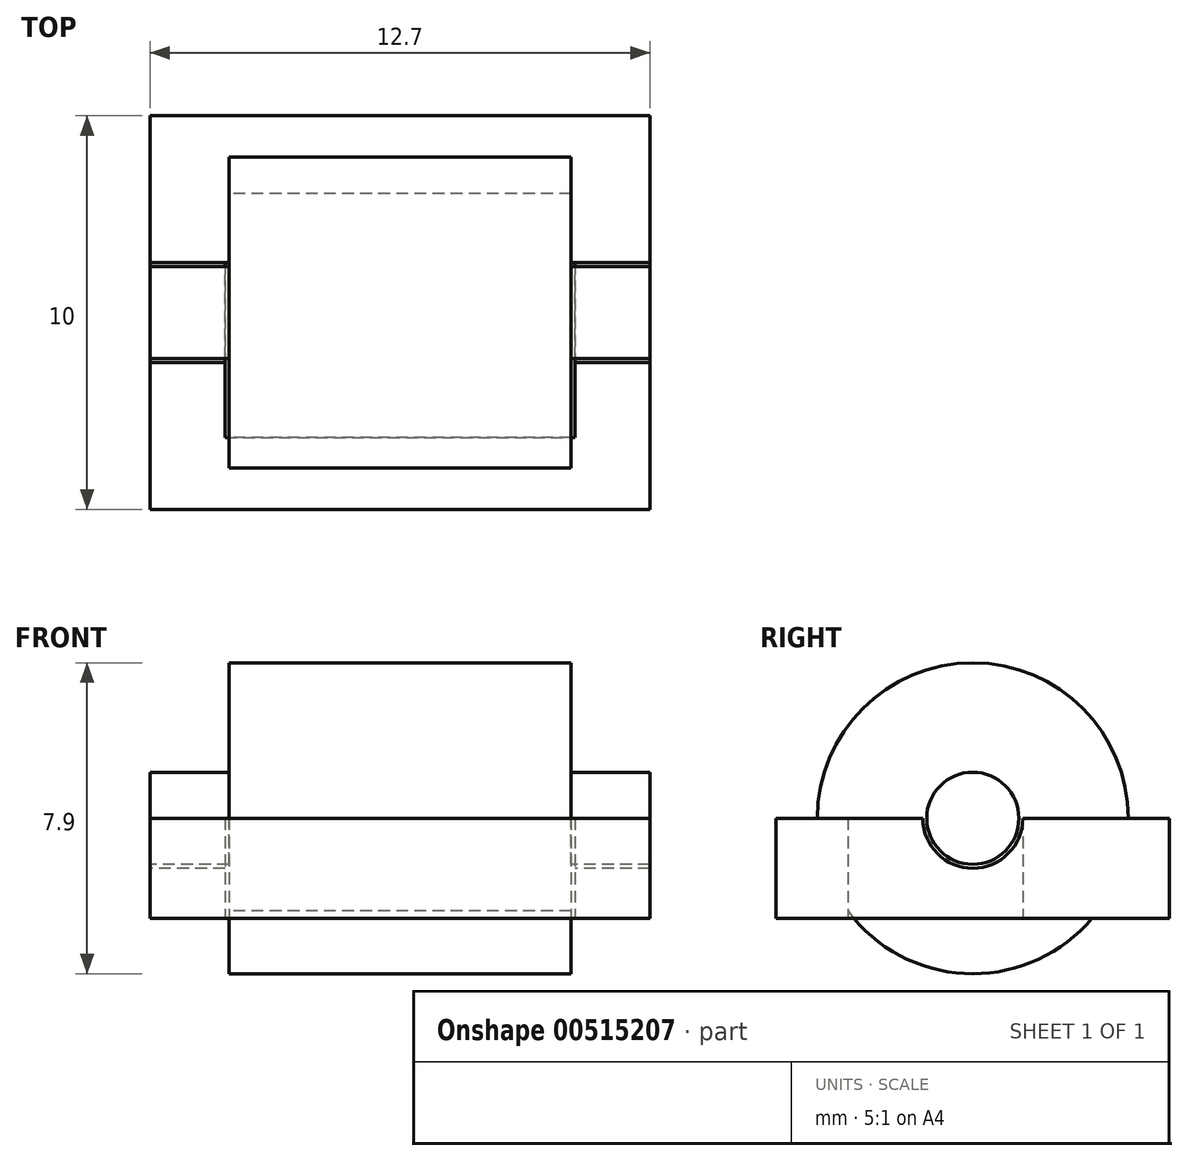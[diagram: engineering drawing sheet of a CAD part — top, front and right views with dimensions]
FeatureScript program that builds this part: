
annotation { "Feature Type Name" : "Feature", "Feature Type Description" : "" }
export const myFeature = defineFeature(function(context is Context, id is Id, definition is map)
    precondition{}
    {
        {
            var Q0;
            Q0=qCreatedBy(makeId("Right.planeOp"),FACE);
            var sketch = newSketch(context, id + "F0", { "sketchPlane" : qUnion([Q0])});
            skLineSegment(sketch, "E0", {"start": v(0, 0) * mm, "end": v(5, 0) * mm});
            skLineSegment(sketch, "E1", {"start": v(5, 0) * mm, "end": v(5, 2.54) * mm});
            skLineSegment(sketch, "E2", {"start": v(5, 2.54) * mm, "end": v(1.27, 2.54) * mm});
            skLineSegment(sketch, "E3", {"start": v(0, 0) * mm, "end": v(-5, 0) * mm});
            skLineSegment(sketch, "E4", {"start": v(-5, 0) * mm, "end": v(-5, 2.54) * mm});
            skLineSegment(sketch, "E5", {"start": v(-5, 2.54) * mm, "end": v(-1.27, 2.54) * mm});
            skArc(sketch, "E6", {"start": v(-1.27, 2.54) * mm, "mid": v(0, 1.27) * mm, "end": v(1.27, 2.54) * mm});
            skLineSegment(sketch, "E7", {"start": v(-1.27, 2.54) * mm, "end": v(1.27, 2.54) * mm, "construction": true});
            skSolve(sketch);
        }
        {
            var Q0;
            Q0=makeQuery(id+"F0.imprint","IMPRINT",FACE,{"disambiguationData":[TD([[makeQuery(id+"F0.imprint","IMPRINT",EDGE,{"derivedFrom":sQuery(id+"F0.wireOp",EDGE,"E0")}),1.0]])]});
            extrude(context, id + "F1", {"entities" : qUnion([Q0]), "depth" : 6.35 * mm, "offsetDistance" : 25.4 * mm, "hasSecondDirection" : true, "secondDirectionOppositeDirection" : true, "secondDirectionDepth" : 6.35 * mm});
        }
        {
            var Q0;
            Q0=qCreatedBy(makeId("Top.planeOp"),FACE);
            var sketch = newSketch(context, id + "F2", { "sketchPlane" : qUnion([Q0])});
            skPoint(sketch, "E8.0", {"position": v(6.35, -1.27) * mm});
            skPoint(sketch, "E8.1", {"position": v(-6.35, 1.27) * mm});
            skLineSegment(sketch, "E9", {"start": v(6.35, -1.27) * mm, "end": v(4.45, -1.27) * mm});
            skLineSegment(sketch, "E10", {"start": v(-6.35, 1.27) * mm, "end": v(-4.45, 1.27) * mm});
            skLineSegment(sketch, "E11.bottom", {"start": v(-4.45, 1.27) * mm, "end": v(4.45, 1.27) * mm});
            skLineSegment(sketch, "E11.top", {"start": v(-4.45, -1.27) * mm, "end": v(4.45, -1.27) * mm});
            skLineSegment(sketch, "E11.left", {"start": v(-4.45, 1.27) * mm, "end": v(-4.45, -1.27) * mm});
            skLineSegment(sketch, "E11.right", {"start": v(4.45, 1.27) * mm, "end": v(4.45, -1.27) * mm});
            skLineSegment(sketch, "E12", {"start": v(4.45, -1.27) * mm, "end": v(4.45, -3.18) * mm, "construction": true});
            skLineSegment(sketch, "E13", {"start": v(-4.45, 1.27) * mm, "end": v(-4.45, 3.18) * mm, "construction": true});
            skLineSegment(sketch, "E14.top", {"start": v(-4.45, -3.18) * mm, "end": v(4.45, -3.18) * mm});
            skLineSegment(sketch, "E14.left", {"start": v(-4.45, -1.27) * mm, "end": v(-4.45, -3.18) * mm});
            skLineSegment(sketch, "E14.right", {"start": v(4.45, -1.27) * mm, "end": v(4.45, -3.18) * mm});
            skLineSegment(sketch, "E15.bottom", {"start": v(4.45, 1.27) * mm, "end": v(-4.45, 1.27) * mm});
            skLineSegment(sketch, "E15.top", {"start": v(4.45, 3.18) * mm, "end": v(-4.45, 3.18) * mm});
            skLineSegment(sketch, "E15.left", {"start": v(4.45, 1.27) * mm, "end": v(4.45, 3.18) * mm});
            skLineSegment(sketch, "E15.right", {"start": v(-4.45, 1.27) * mm, "end": v(-4.45, 3.18) * mm});
            skSolve(sketch);
        }
        {
            var Q0;
            Q0=makeQuery(id+"F2.imprint","IMPRINT",FACE,{"disambiguationData":[TD([[makeQuery(id+"F2.imprint","IMPRINT",EDGE,{"derivedFrom":sQuery(id+"F2.wireOp",EDGE,"E11.top")}),-1.0]])]});
            var Q1;
            Q1=makeQuery(id+"F2.imprint","IMPRINT",FACE,{"disambiguationData":[TD([[makeQuery(id+"F2.imprint","IMPRINT",EDGE,{"derivedFrom":sQuery(id+"F2.wireOp",EDGE,"E11.left")}),1.0]])]});
            var Q2;
            Q2=makeQuery(id+"F2.imprint","IMPRINT",FACE,{"disambiguationData":[TD([[makeQuery(id+"F2.imprint","IMPRINT",EDGE,{"derivedFrom":sQuery(id+"F2.wireOp",EDGE,"E15.bottom")}),-1.0]])]});
            extrude(context, id + "F3", {"entities" : qUnion([Q0, Q1, Q2]), "operationType" : NewBodyOperationType.REMOVE, "endBound" : BoundingType.UP_TO_NEXT, "depth" : 25.4 * mm, "offsetDistance" : 25.4 * mm});
        }
        {
            var Q0;
            Q0=qCreatedBy(makeId("Right.planeOp"),FACE);
            var sketch = newSketch(context, id + "F4", { "sketchPlane" : qUnion([Q0])});
            skArc(sketch, "E16.0", {"start": v(-1.27, 2.54) * mm, "mid": v(0, 1.27) * mm, "end": v(1.27, 2.54) * mm, "construction": true});
            skCircle(sketch, "E17", {"center": v(0, 2.54) * mm, "radius": 1.17 * mm});
            skSolve(sketch);
        }
        {
            var Q0;
            Q0 = qSketchRegion(id + "F4", true);
            extrude(context, id + "F5", {"entities" : qUnion([Q0]), "depth" : 6.35 * mm, "offsetDistance" : 25.4 * mm, "hasSecondDirection" : true, "secondDirectionOppositeDirection" : true, "secondDirectionDepth" : 6.35 * mm});
        }
        {
            var Q0;
            Q0=qCreatedBy(makeId("Right.planeOp"),FACE);
            var sketch = newSketch(context, id + "F6", { "sketchPlane" : qUnion([Q0])});
            skPoint(sketch, "E18.0", {"position": v(-3.18, 2.54) * mm});
            skPoint(sketch, "E18.1", {"position": v(3.18, 2.54) * mm});
            skCircle(sketch, "E19.0", {"center": v(0, 2.54) * mm, "radius": 1.17 * mm, "construction": true});
            skCircle(sketch, "E20", {"center": v(0, 2.54) * mm, "radius": 3.95 * mm});
            skSolve(sketch);
        }
        {
            var Q0;
            Q0=makeQuery(id+"F6.imprint","IMPRINT",FACE,{"disambiguationData":[TD([[makeQuery(id+"F6.imprint","IMPRINT",EDGE,{"derivedFrom":sQuery(id+"F6.wireOp",EDGE,"E20")}),1.0]])]});
            var Q1;
            Q1=makeQuery(id+"F3.boolean.opBoolean","COPY",FACE,{"derivedFrom":makeQuery(id+"F3.opExtrude","SWEPT_FACE",FACE,{"disambiguationData":[OSD([sQuery(id+"F2.wireOp",EDGE,"E11.right"),sQuery(id+"F2.wireOp",EDGE,"E14.right"),sQuery(id+"F2.wireOp",EDGE,"E15.left")])]})});
            var Q2;
            Q2=makeQuery(id+"F3.boolean.opBoolean","COPY",FACE,{"derivedFrom":makeQuery(id+"F3.opExtrude","SWEPT_FACE",FACE,{"disambiguationData":[OSD([sQuery(id+"F2.wireOp",EDGE,"E11.left"),sQuery(id+"F2.wireOp",EDGE,"E14.left"),sQuery(id+"F2.wireOp",EDGE,"E15.right")])]})});
            extrude(context, id + "F7", {"entities" : qUnion([Q0]), "operationType" : NewBodyOperationType.ADD, "endBound" : BoundingType.UP_TO_SURFACE, "depth" : 25.4 * mm, "endBoundEntityFace" : qUnion([Q1]), "hasOffset" : true, "offsetDistance" : .1 * mm, "hasSecondDirection" : true, "secondDirectionBound" : BoundingType.UP_TO_SURFACE, "secondDirectionOppositeDirection" : true, "secondDirectionDepth" : 25.4 * mm, "secondDirectionBoundEntityFace" : qUnion([Q2]), "hasSecondDirectionOffset" : true, "secondDirectionOffsetDistance" : .1 * mm});
        }
    });
